# Revit family: Light with a table_LivingDivaniBIM
name_source: partatom
category: Apparecchi per illuminazione
revit_build: Autodesk Revit 2017 (Build: 20190508_0315(x64)
units: mm (PartAtom-declared; Revit-internal decimal feet)

## family parameters
Basato su piano di lavoro = No
Condiviso = No
Numero OmniClass = 23.80.00.00
Punto di calcolo locali = No
Quota connettore circolare = Usa diametro
Sempre verticale = Sì
Sorgente d'illuminazione = Sì
Taglio con vuoti quando caricato = No
Tipo di parte = Normale
Titolo OmniClass = Electric Power and Lighting

## types (1)
- Light with a table_LivingDivaniBIM
    Codice Prodotto = LWT190LT
    Dimensioni simbolo sorgente d'illuminazione = 610 mm
    Filtro dei colori = 16777215
    Materiale = Legno LivingDivani
    Materiale lampadina = Plastica bianca
    Materiale struttura = Metallo LivingDivani
    Modello = Light with a table
    Produttore = Living Divani
    URL = www.livingdivani.it
    Variazione temperatura colore lampada con luminosità attenuata = <Nessuno>
